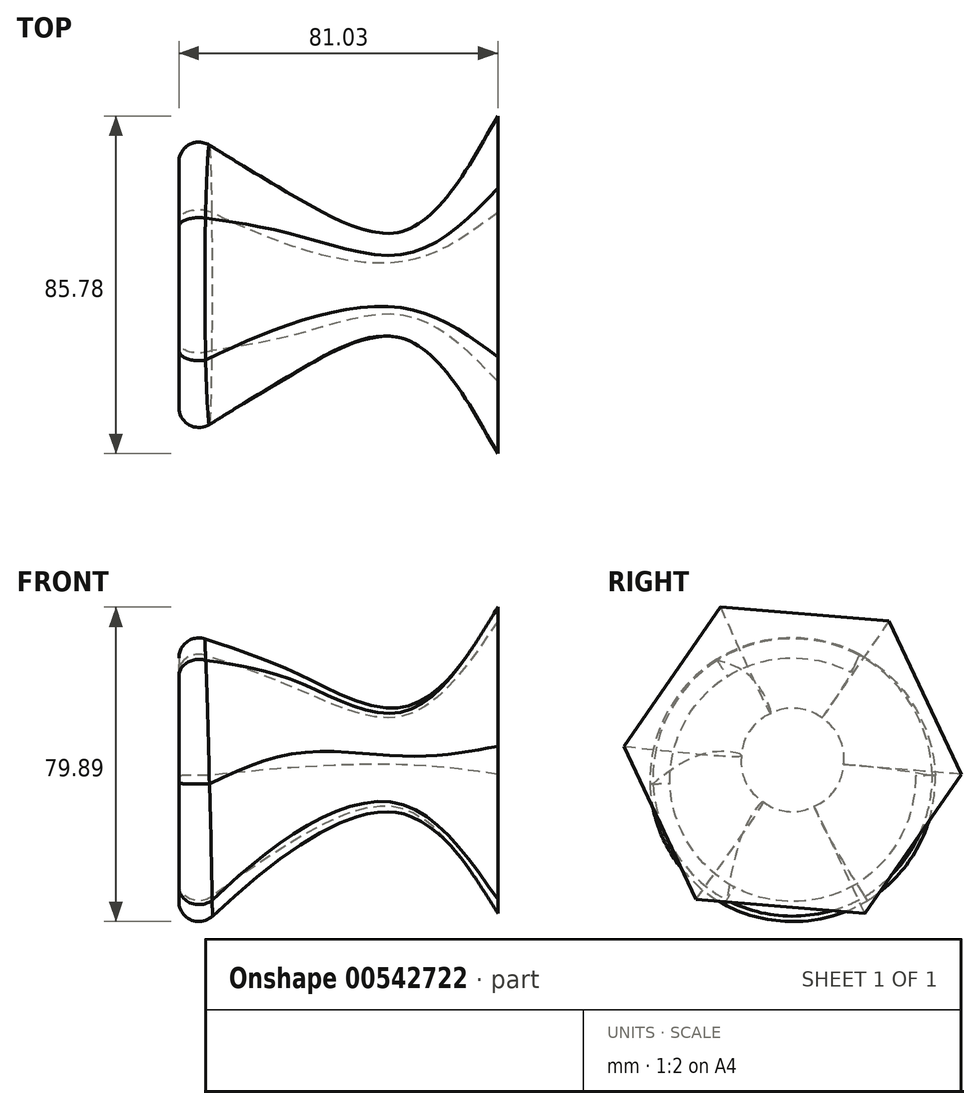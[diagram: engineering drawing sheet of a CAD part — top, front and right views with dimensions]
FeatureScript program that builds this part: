
annotation { "Feature Type Name" : "Feature", "Feature Type Description" : "" }
export const myFeature = defineFeature(function(context is Context, id is Id, definition is map)
    precondition{}
    {
        {
            var Q0;
            Q0=qCreatedBy(makeId("Right.planeOp"),FACE);
            cPlane(context, id + "F0", {"entities" : qUnion([Q0]), "cplaneType" : CPlaneType.OFFSET, "offset" : 25.4 * mm, "width" : 152.4 * mm, "height" : 152.4 * mm});
        }
        {
            var Q0;
            Q0=qCreatedBy(id+"F0.planeOp",FACE);
            cPlane(context, id + "F1", {"entities" : qUnion([Q0]), "cplaneType" : CPlaneType.OFFSET, "offset" : 25.4 * mm, "width" : 152.4 * mm, "height" : 152.4 * mm});
        }
        {
            var Q0;
            Q0=qCreatedBy(makeId("Right.planeOp"),FACE);
            cPlane(context, id + "F2", {"entities" : qUnion([Q0]), "cplaneType" : CPlaneType.OFFSET, "offset" : 30.23 * mm, "oppositeDirection" : true, "width" : 152.4 * mm, "height" : 152.4 * mm});
        }
        {
            var Q0;
            Q0=qCreatedBy(id+"F1.planeOp",FACE);
            var sketch = newSketch(context, id + "F3", { "sketchPlane" : qUnion([Q0])});
            skCircle(sketch, "E0.cCircle", {"center": v(0, 0) * mm, "radius": 43.04 * mm, "construction": true});
            skLineSegment(sketch, "E0.0", {"start": v(24.52, 35.37) * mm, "end": v(42.9, -3.55) * mm});
            skLineSegment(sketch, "E0.1", {"start": v(42.9, -3.55) * mm, "end": v(18.37, -38.92) * mm});
            skLineSegment(sketch, "E0.2", {"start": v(18.37, -38.92) * mm, "end": v(-24.52, -35.37) * mm});
            skLineSegment(sketch, "E0.3", {"start": v(-24.52, -35.37) * mm, "end": v(-42.9, 3.55) * mm});
            skLineSegment(sketch, "E0.4", {"start": v(-42.9, 3.55) * mm, "end": v(-18.37, 38.92) * mm});
            skLineSegment(sketch, "E0.5", {"start": v(-18.37, 38.92) * mm, "end": v(24.52, 35.37) * mm});
            skSolve(sketch);
        }
        {
            var Q0;
            Q0=qCreatedBy(makeId("Right.planeOp"),FACE);
            var sketch = newSketch(context, id + "F4", { "sketchPlane" : qUnion([Q0])});
            skCircle(sketch, "E1", {"center": v(0, 0) * mm, "radius": 21.94 * mm});
            skSolve(sketch);
        }
        {
            var Q0;
            Q0=qCreatedBy(id+"F0.planeOp",FACE);
            var sketch = newSketch(context, id + "F5", { "sketchPlane" : qUnion([Q0])});
            skCircle(sketch, "E2", {"center": v(0, 0) * mm, "radius": 13.31 * mm});
            skSolve(sketch);
        }
        {
            var Q0;
            Q0=qCreatedBy(id+"F2.planeOp",FACE);
            var sketch = newSketch(context, id + "F6", { "sketchPlane" : qUnion([Q0])});
            skCircle(sketch, "E3", {"center": v(0, -7.38) * mm, "radius": 40.37 * mm});
            skSolve(sketch);
        }
        {
            var Q0;
            Q0=makeQuery(id+"F3.imprint","IMPRINT",FACE,{"disambiguationData":[TD([[makeQuery(id+"F3.imprint","IMPRINT",EDGE,{"derivedFrom":sQuery(id+"F3.wireOp",EDGE,"E0.0")}),-1.0]])]});
            var Q1;
            Q1=makeQuery(id+"F5.imprint","IMPRINT",FACE,{"disambiguationData":[TD([[makeQuery(id+"F5.imprint","IMPRINT",EDGE,{"derivedFrom":sQuery(id+"F5.wireOp",EDGE,"E2")}),1.0]])]});
            var Q2;
            Q2=makeQuery(id+"F4.imprint","IMPRINT",FACE,{"disambiguationData":[TD([[makeQuery(id+"F4.imprint","IMPRINT",EDGE,{"derivedFrom":sQuery(id+"F4.wireOp",EDGE,"E1")}),1.0]])]});
            var Q3;
            Q3=makeQuery(id+"F6.imprint","IMPRINT",FACE,{"disambiguationData":[TD([[makeQuery(id+"F6.imprint","IMPRINT",EDGE,{"derivedFrom":sQuery(id+"F6.wireOp",EDGE,"E3")}),1.0]])]});
            loft(context, id + "F7", {"sheetProfilesArray" : [{ "sheetProfileEntities" : qUnion([Q0]) }, { "sheetProfileEntities" : qUnion([Q1]) }, { "sheetProfileEntities" : qUnion([Q2]) }, { "sheetProfileEntities" : qUnion([Q3]) }]});
        }
        {
            var Q0;
            Q0=makeQuery(id+"F7.opLoft","MID_CAP_EDGE",EDGE,{"disambiguationData":[OSD([sQuery(id+"F3.wireOp",EDGE,"E0.2"),sQuery(id+"F3.wireOp",EDGE,"E0.3"),sQuery(id+"F3.wireOp",EDGE,"E0.4"),sQuery(id+"F6.wireOp",EDGE,"E3")])],"capPos":3.0});
            var Q1;
            Q1=makeQuery(id+"F7.opLoft","MID_CAP_EDGE",EDGE,{"disambiguationData":[OSD([sQuery(id+"F3.wireOp",EDGE,"E0.0"),sQuery(id+"F3.wireOp",EDGE,"E0.3"),sQuery(id+"F3.wireOp",EDGE,"E0.4"),sQuery(id+"F3.wireOp",EDGE,"E0.5"),sQuery(id+"F6.wireOp",EDGE,"E3")])],"capPos":3.0});
            var Q2;
            Q2=makeQuery(id+"F7.opLoft","MID_CAP_EDGE",EDGE,{"disambiguationData":[OSD([sQuery(id+"F3.wireOp",EDGE,"E0.0"),sQuery(id+"F3.wireOp",EDGE,"E0.5"),sQuery(id+"F6.wireOp",EDGE,"E3")])],"capPos":3.0});
            var Q3;
            Q3=makeQuery(id+"F7.opLoft","MID_CAP_EDGE",EDGE,{"disambiguationData":[OSD([sQuery(id+"F3.wireOp",EDGE,"E0.0"),sQuery(id+"F3.wireOp",EDGE,"E0.1"),sQuery(id+"F3.wireOp",EDGE,"E0.5"),sQuery(id+"F6.wireOp",EDGE,"E3")])],"capPos":3.0});
            var Q4;
            Q4=makeQuery(id+"F7.opLoft","MID_CAP_EDGE",EDGE,{"disambiguationData":[OSD([sQuery(id+"F3.wireOp",EDGE,"E0.0"),sQuery(id+"F3.wireOp",EDGE,"E0.1"),sQuery(id+"F3.wireOp",EDGE,"E0.2"),sQuery(id+"F6.wireOp",EDGE,"E3")])],"capPos":3.0});
            fillet(context, id + "F8", {"entities" : qUnion([Q0, Q1, Q2, Q3, Q4]), "radius" : 5.08 * mm, "tangentPropagation" : true, "allowEdgeOverflow" : false});
        }
    });
